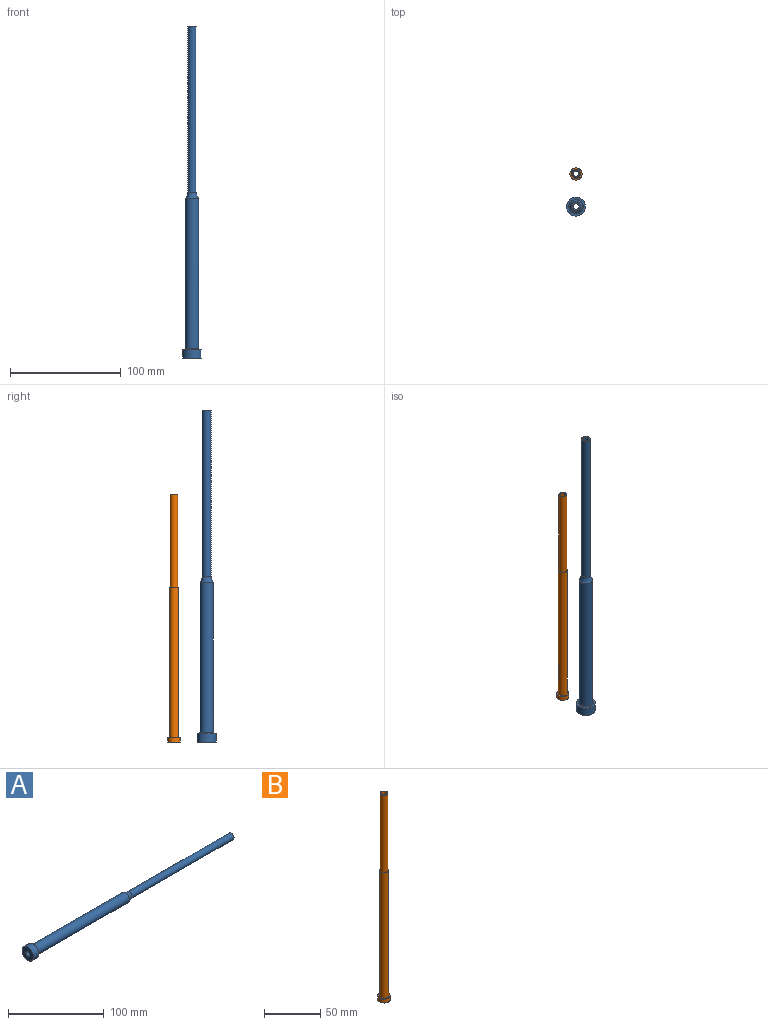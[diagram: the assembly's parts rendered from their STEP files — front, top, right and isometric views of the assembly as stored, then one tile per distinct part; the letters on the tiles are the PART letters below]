
ASSEMBLY  parts=2 mates=1
PART A: 9 faces, bbox 300x17x17 mm
  f0: cylinder r=2.75mm len=300mm, axis (1,0,0), area 5183.6mm2, adj f5,f8
  f1: torus R=6.5mm, axis (-1,0,0), area 30.5mm2, adj f2,f3
  f2: cylinder r=6mm len=135.5mm, axis (1,0,0), area 5108.2mm2, adj f1,f6
  f3: plane 17x17mm, normal (1,0,0), area 94.2mm2, adj f1,f7
  f4: cylinder r=4mm len=150mm, axis (1,0,0), area 3769.9mm2, adj f5,f6
  f5: plane 8x8mm, normal (1,0,0), area 26.5mm2, adj f0,f4
  f6: torus R=14mm, axis (1,0,0), area 189.1mm2, adj f2,f4
  f7: cylinder r=8.5mm len=17mm, axis (1,0,0), area 427.3mm2, adj f3,f8
  f8: plane 17x17mm, normal (-1,0,0), area 203.2mm2, adj f0,f7
PART B: 8 faces, bbox 11x11.2x223.6 mm
  f0: plane 11.2x11.01mm, normal (0,0,-1), area 73mm2, adj f1,f2
  f1: cylinder r=5.5mm len=11mm, axis (0,0,1), area 138.2mm2, adj f0,f3
  f2: cylinder r=2.65mm len=223.57mm, axis (0,0,-1), area 3722.6mm2, adj f0,f4
  f3: plane 11.2x11.01mm, normal (0,0,1), area 44.8mm2, adj f1,f5
  f4: plane 7.09x7mm, normal (0,0,1), area 16.4mm2, adj f2,f6
  f5: cylinder r=4mm len=136mm, axis (0,0,-1), area 3418.1mm2, adj f3,f7
  f6: cylinder r=3.5mm len=83.57mm, axis (0,0,-1), area 1837.8mm2, adj f4,f7
  f7: plane 8.15x8.01mm, normal (0,0,1), area 11.8mm2, adj f5,f6
PLACE A rot(axis=(0.71,0,0.71),180deg) t=(27.52,-11.98,-91.64)mm
PLACE B t=(213.36,165.43,108.36)mm
MATE planar A.f0 <-> B.f0  axis (0,0,-1) through (27.52,-11.98,-91.64)mm
